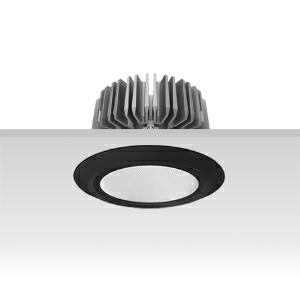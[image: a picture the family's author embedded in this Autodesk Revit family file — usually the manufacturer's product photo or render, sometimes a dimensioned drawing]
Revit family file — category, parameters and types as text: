
# Revit family: 3f_filippi_-_3f_reno_bianco_ampio_3f_filippi_-_30375_a01047_-_3f_reno_150_wh_2000-840_dali_wide___smp_bk_457e
name_source: partatom
category: Lighting Fixtures
units: mm (PartAtom-declared; Revit-internal decimal feet)

## family parameters
Cut with Voids When Loaded = No
Host = Face
Light Source = No
Part Type = Normal
Room Calculation Point = No
Round Connector Dimension = Use Diameter
Shared = No

## types (1)
- 3F Filippi - 3F Reno Bianco Ampio (1 x LED, 1726 lm, 20 W, 4000 K)
    Apparent Load = 20 VA
    Approval mark = CE
    CIE Flux Codes = 73 92 98 100 100
    Color Rendering = 80
    Color Temperature = 4000 K
    Control Gear = Electronic transformer
    Default Elevation = 1800 mm
    Description = ILLUMINOTECHNICAL
Luminous efficiency 100% (DLOR 100%, ULOR 0%).
Initial luminous flux of the luminaire 1726 lm.
Direct symmetric wide distribution.
Installation Interdistance Transv.D = 1.01 x hu - Long.D = 1.00 x hu.
Tabular UGR (CIE 117 - 4H-8H; S=0.25H; 70/50/20): RUG 23.4 - 23.4.
Beam angle: 70° - 70°.
Luminous efficacy 86 lm/W.
Lifetime (L90/B10): 30000 h. (tq+25°C)
Lifetime (L85/B10): 50000 h. (tq+25°C)
Lifetime (L70/B10): 80000 h. (tq+25°C)
Sudden decreased luminous flux after 50000 hours: 0% (C0).
Photobiological safety in compliance with IEC/TR 62778: RG0 risk exempt, (IEC 62471).
In compliance with IEC/EN 62722-2-1 - IEC/EN 62717 standards.

SOURCE
Compact LED module 2000/840.
Energy efficiency class (UE 2019/2020 - UE 2019/2015): D.
CIE 13.3 Colour rendering index: CRI >80 (R9 <50%).
IES TM-30 Fidelity Index: Rf = 84 Rg = 95.
CCT nominal colour temperature 4000 K.
Colour initial tolerance (MacAdam): SDCM 3.
Zhaga Book 3 compliant.

MECHANICAL
Passive heat dissipator in die-casting aluminium, oversized, for optimum thermal management of the LED module.
Parabolic element with graduated/concentric rings in white polycarbonate.
Transparent external lens with glossy and satin differentiated surfaces, with a cooling and anti-insect system in methacrylate (PMMA).
Fastening spring clips in stainless steel.
Dimensions: diameter 176 mm, height 111 mm. Weight 0.78 kg.
IP44 protection degree for exposed part, IP20 for recessed part.
Mechanical strength to impacts IK05 (0.7 joule).
Glow-wire test resistance 650°C.

ELECTRICAL
Wiring on a separate unit.
Halogen Free DALI-2 DATI (Parts 251, 252, 253), PUSH-DIM, electronic wiring 230V-50/60Hz, power factor 0.90 at full load, THD <25%, constant output current, SELV, class II, 1 driver, 1 DALI addresse.
Power of the luminaire 20 W.
ENEC - CE.
SAFE FLICKER: PstLM=<1 and SVM=<0.4 (IEC TR 61547-1 and IEC TR 63158), to ensure a more comfortable and safe light.
Luminaire compliant with EN 60598-2-22 for power supply from a centralised emergency system CPSS (Central Power Supply System), not incorporated in the luminaire - high risk areas excluded. The default power and flux are 100% in AC and 100% in DC.
Ambient temperature from 0°C to +25°C.
Temperature class T6 max 85°C.
Relative humidity UR: <85%.

INSTALLATION
Pull-up recessed fitting.
False ceiling carving: 150 mm.
All accessories dedicated to this product are available on the Catalog and on our website www.3F-Filippi.com.

ACCESSORIES
A01047 - Anti-glare microprismatic SMP diffuser in methacrylate (PMMA), locked and in line with the trim, in black polycarbonate.

APPLICATIONS
Suitable product for food production plants (HACCP), IFS (Food Version 6), BRC (GSFS Food Version 7).
Environments: architectural, commercial, exhibition areas, transit areas, corridors, shops, display windows, service areas.
In false ceilings with narrow voids.

LIGHT MANAGEMENT
Recommended minimum setting: 10%.
The luminaire, equipped with (DALI-2 DATI) driver, can be controlled manually with 3F Easy Dim technology or automatically/manually with wired or wireless DALI/D2D control systems.
The D2D driver guarantees interoperability with other devices with the same certification by making the following information available:
Device Data (Part 251), Energy Report (Part 252), Diagnosis & Maintenance (Part 253).
In electrical systems without a regulation system (manual or automatic) and DALI bus, a suitable jumper must be made on the DA-DA terminals of the appliance.

WARNING
Luminaire designed for disposal/recycling at end-of-life.
Replaceable (LED only) light source by a professional. Replaceable control gear by a professional.
    Height = 0 mm  [stored 0 ft]
    Lamp = 1 x LED
    Lamp Light Flux = 1726 lm
    Lamp Power = 20 W
    Lamp count = 1
    Length = 176 mm
    Lifetime = 50000 h
    Luminous efficacy = 86 lm/W
    Manufacturer = 3F Filippi
    ModVariant = No
    Model = 3F Filippi - 30375+A01047 - 3F Reno 150 WH 2000-840 DALI WIDE + SMP BK
    Mounting Place = Ceiling
    Mounting Type = Recessed
    Number of Poles = 1
    OnlyDefault = Yes
    Power Factor = 1
    Product Name = 3F Filippi - 3F Reno Bianco Ampio
    Product group = recessed luminaire
    ProductGroupID = 4
    Protection Class = Protection class II
    Protection Degree = IP 20
    RLX_Detail_Level = 1
    RLX_Emergency_Light_Flux = 0 lm
    RLX_Emergency_Type = 0
    RLX_Emergency_Type_DB = No
    RlxData = <blob elided: 88393 chars, md5=6c6455b7>
    Socket = socket
    Standby Power = 0 W
    System Light Flux = 1726 lm
    System Power = 20 W
    Type Comments = Product without accessories
    Type Image = 3ffilippi_3f_reno_150_bk_vs_smp.jpg
    URL = http://relux.com
    VarID = ---
    Voltage = 0 V
    Weight = 0.00 kg
    Width = 0 mm  [stored 0 ft]

note: [stored X ft] marks values corroborated as IEEE doubles in the binary element streams (Revit-internal decimal feet)

## geometry (parser evidence)
native form markers: Blend x4, Sweep x11
no freeform markers — native parametric forms only
